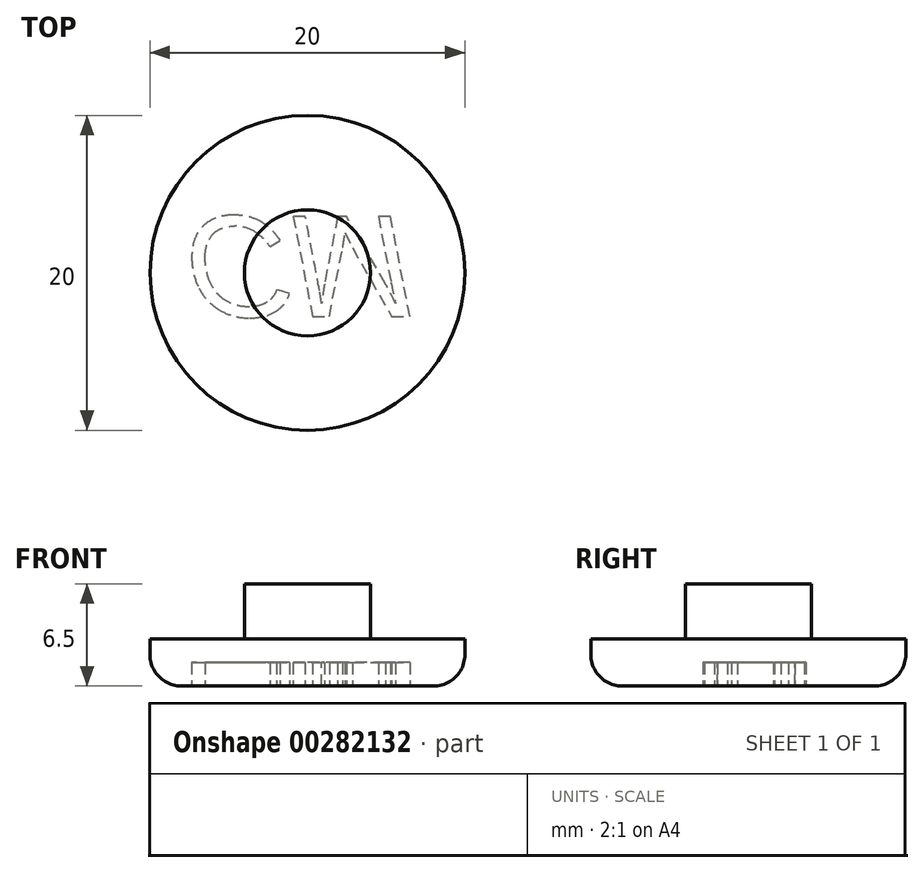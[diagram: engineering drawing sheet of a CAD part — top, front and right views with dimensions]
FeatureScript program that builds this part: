
annotation { "Feature Type Name" : "Feature", "Feature Type Description" : "" }
export const myFeature = defineFeature(function(context is Context, id is Id, definition is map)
    precondition{}
    {
        {
            var Q0;
            Q0=qCreatedBy(makeId("Top.planeOp"),FACE);
            var sketch = newSketch(context, id + "F0", { "sketchPlane" : qUnion([Q0])});
            skCircle(sketch, "E0", {"center": v(0, 0) * mm, "radius": 10 * mm});
            skSolve(sketch);
        }
        {
            var Q0;
            Q0=qSketchRegion(id+"F0",true);
            extrude(context, id + "F1", {"entities" : qUnion([Q0]), "depth" : 3 * mm});
        }
        {
            var Q0;
            Q0=makeQuery(id+"F1.opExtrude","CAP_FACE",FACE,{"disambiguationData":[OSD([sQuery(id+"F0.wireOp",EDGE,"E0")])],"isStart":false});
            var sketch = newSketch(context, id + "F2", { "sketchPlane" : qUnion([Q0])});
            skCircle(sketch, "E1", {"center": v(0, 0) * mm, "radius": 4 * mm});
            skSolve(sketch);
        }
        {
            var Q0;
            Q0=qSketchRegion(id+"F2",true);
            extrude(context, id + "F3", {"entities" : qUnion([Q0]), "operationType" : NewBodyOperationType.ADD, "depth" : 3.5 * mm});
        }
        {
            var Q0;
            Q0=makeQuery(id+"F1.opExtrude","CAP_EDGE",EDGE,{"disambiguationData":[OSD([sQuery(id+"F0.wireOp",EDGE,"E0")])],"isStart":true});
            fillet(context, id + "F4", {"entities" : qUnion([Q0]), "radius" : 2 * mm, "tangentPropagation" : true, "allowEdgeOverflow" : false});
        }
        {
            var Q0;
            Q0=makeQuery(id+"F1.opExtrude","CAP_FACE",FACE,{"disambiguationData":[OSD([sQuery(id+"F0.wireOp",EDGE,"E0")])],"isStart":true});
            var sketch = newSketch(context, id + "F5", { "sketchPlane" : qUnion([Q0])});
            skText(sketch, "E2", { "text": "CM", "fontName": "Arimo-Italic.ttf"});
            const initialGuessF5  = {"E2": [-0.00786, -0.00358, 1, 0, 0.00665]};
            skSetInitialGuess(sketch, initialGuessF5);
            skSolve(sketch);
        }
        {
            var Q0;
            Q0 = qSketchRegion(id + "F5", true);
            extrude(context, id + "F6", {"entities" : qUnion([Q0]), "operationType" : NewBodyOperationType.REMOVE, "oppositeDirection" : true, "depth" : 1.5 * mm});
        }
    });
